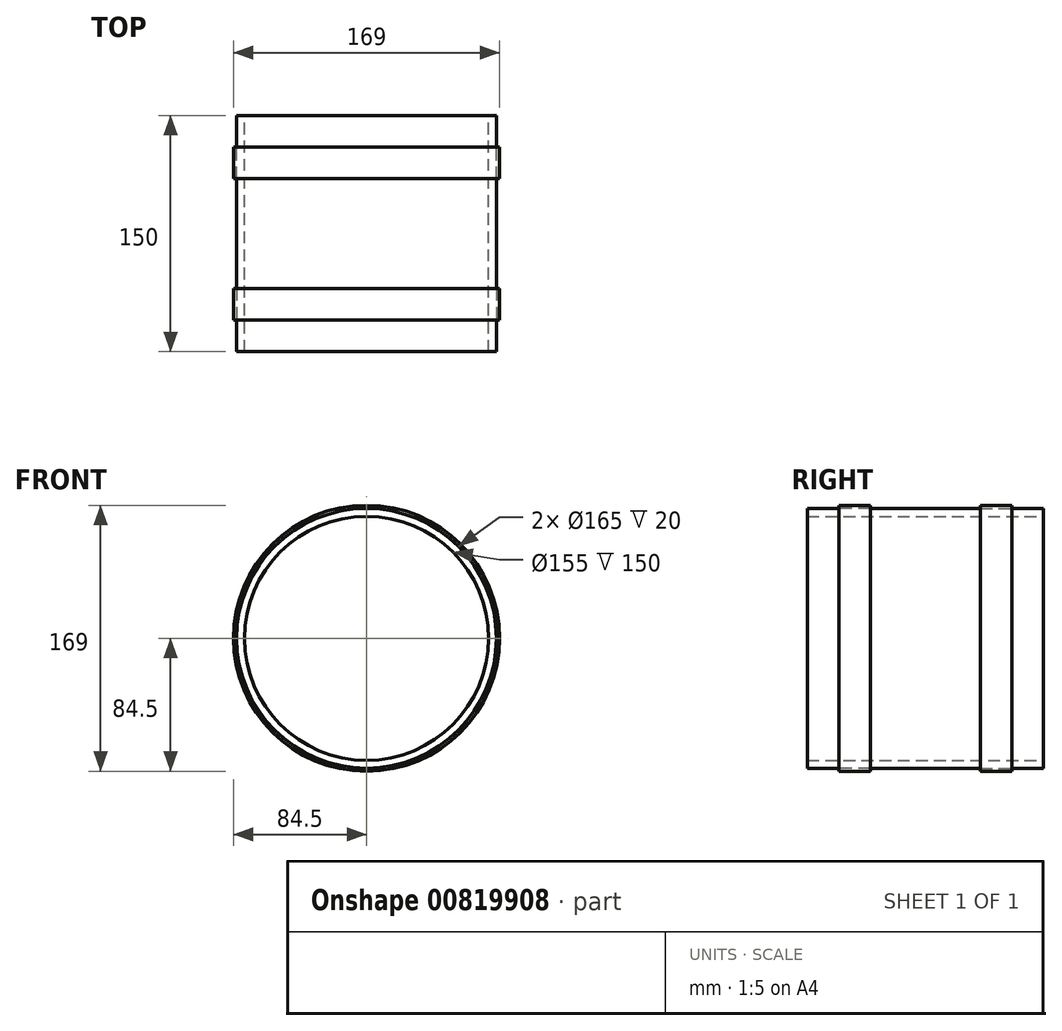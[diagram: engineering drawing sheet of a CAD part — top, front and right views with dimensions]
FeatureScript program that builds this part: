
annotation { "Feature Type Name" : "Feature", "Feature Type Description" : "" }
export const myFeature = defineFeature(function(context is Context, id is Id, definition is map)
    precondition{}
    {
        {
            var Q0;
            Q0=qCreatedBy(makeId("Front.planeOp"),FACE);
            var sketch = newSketch(context, id + "F0", { "sketchPlane" : qUnion([Q0])});
            skCircle(sketch, "E0", {"center": v(0, 0) * mm, "radius": 77.5 * mm});
            skCircle(sketch, "E1", {"center": v(0, 0) * mm, "radius": 82.5 * mm});
            skSolve(sketch);
        }
        {
            var Q0;
            Q0=qSketchRegion(id+"F0",true);
            extrude(context, id + "F1", {"entities" : qUnion([Q0]), "depth" : 150 * mm, "offsetDistance" : 25 * mm});
        }
        {
            var Q0;
            Q0=makeQuery(id+"F1.opExtrude","CAP_FACE",FACE,{"disambiguationData":[OSD([sQuery(id+"F0.wireOp",EDGE,"E0"),sQuery(id+"F0.wireOp",EDGE,"E1")])],"isStart":false});
            var sketch = newSketch(context, id + "F2", { "sketchPlane" : qUnion([Q0])});
            skCircle(sketch, "E2", {"center": v(0, 0) * mm, "radius": 82.5 * mm});
            skCircle(sketch, "E3", {"center": v(0, 0) * mm, "radius": 84.5 * mm});
            skSolve(sketch);
        }
        {
            var Q0;
            Q0=makeQuery(id+"F2.imprint","IMPRINT",FACE,{"disambiguationData":[TD([[makeQuery(id+"F2.imprint","IMPRINT",EDGE,{"derivedFrom":sQuery(id+"F2.wireOp",EDGE,"E2")}),-1.0]])]});
            extrude(context, id + "F3", {"entities" : qUnion([Q0]), "oppositeDirection" : true, "depth" : 40 * mm, "offsetDistance" : 25 * mm});
        }
        {
            var Q0;
            Q0=makeQuery(id+"F3.opExtrude","CAP_FACE",FACE,{"disambiguationData":[OSD([sQuery(id+"F2.wireOp",EDGE,"E2"),sQuery(id+"F2.wireOp",EDGE,"E3")])],"isStart":true});
            extrude(context, id + "F4", {"entities" : qUnion([Q0]), "operationType" : NewBodyOperationType.REMOVE, "oppositeDirection" : true, "depth" : 20 * mm, "offsetDistance" : 25 * mm});
        }
        {
            var Q0;
            Q0=makeQuery(id+"F1.opExtrude","CAP_FACE",FACE,{"disambiguationData":[OSD([sQuery(id+"F0.wireOp",EDGE,"E0"),sQuery(id+"F0.wireOp",EDGE,"E1")])],"isStart":true});
            var sketch = newSketch(context, id + "F5", { "sketchPlane" : qUnion([Q0])});
            skCircle(sketch, "E4", {"center": v(0, 0) * mm, "radius": 82.5 * mm});
            skCircle(sketch, "E5", {"center": v(0, 0) * mm, "radius": 84.5 * mm});
            skSolve(sketch);
        }
        {
            var Q0;
            Q0=makeQuery(id+"F5.imprint","IMPRINT",FACE,{"disambiguationData":[TD([[makeQuery(id+"F5.imprint","IMPRINT",EDGE,{"derivedFrom":sQuery(id+"F5.wireOp",EDGE,"E4")}),1.0]])]});
            extrude(context, id + "F6", {"entities" : qUnion([Q0]), "oppositeDirection" : true, "depth" : 40 * mm, "offsetDistance" : 25 * mm});
        }
        {
            var Q0;
            Q0=qSketchRegion(id+"F5",true);
            var Q1;
            Q1=makeQuery(id+"F6.opExtrude","CAP_FACE",FACE,{"disambiguationData":[OSD([sQuery(id+"F5.wireOp",EDGE,"E4"),sQuery(id+"F5.wireOp",EDGE,"E5")])],"isStart":true});
            extrude(context, id + "F7", {"entities" : qUnion([Q0, Q1]), "operationType" : NewBodyOperationType.REMOVE, "oppositeDirection" : true, "depth" : 20 * mm, "offsetDistance" : 25 * mm});
        }
    });
